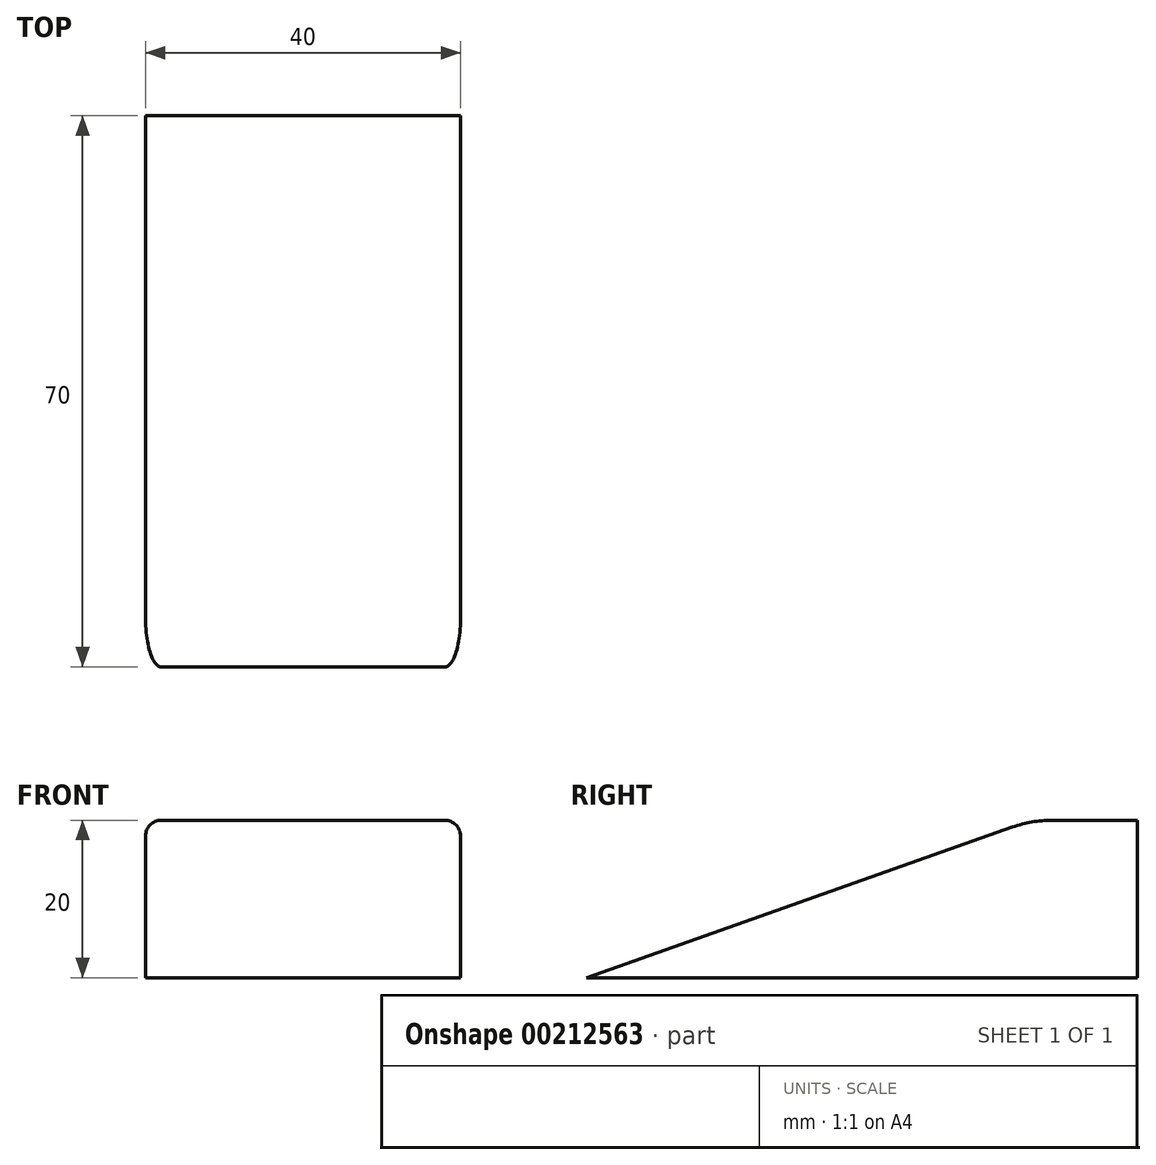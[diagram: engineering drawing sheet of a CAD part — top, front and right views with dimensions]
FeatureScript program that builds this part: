
annotation { "Feature Type Name" : "Feature", "Feature Type Description" : "" }
export const myFeature = defineFeature(function(context is Context, id is Id, definition is map)
    precondition{}
    {
        {
            var Q0;
            Q0=qCreatedBy(makeId("Right.planeOp"),FACE);
            var sketch = newSketch(context, id + "F0", { "sketchPlane" : qUnion([Q0])});
            skLineSegment(sketch, "E0.bottom", {"start": v(20.03, 15.08) * mm, "end": v(33.47, 15.08) * mm});
            skLineSegment(sketch, "E0.top", {"start": v(-36.53, -4.92) * mm, "end": v(33.47, -4.92) * mm});
            skLineSegment(sketch, "E0.right", {"start": v(33.47, 15.08) * mm, "end": v(33.47, -4.92) * mm});
            skLineSegment(sketch, "E1", {"start": v(-36.53, -4.92) * mm, "end": v(20.03, 15.08) * mm});
            skSolve(sketch);
        }
        {
            var Q0;
            Q0=makeQuery(id+"F0.imprint","IMPRINT",FACE,{"disambiguationData":[TD([[makeQuery(id+"F0.imprint","IMPRINT",EDGE,{"derivedFrom":sQuery(id+"F0.wireOp",EDGE,"E0.bottom")}),-1.0]])]});
            extrude(context, id + "F1", {"entities" : qUnion([Q0]), "depth" : 40 * mm});
        }
        {
            var Q0;
            Q0=makeQuery(id+"F1.opExtrude","SWEPT_EDGE",EDGE,{"disambiguationData":[OSD([sQuery(id+"F0.wireOp",EDGE,"E0.bottom"),sQuery(id+"F0.wireOp",EDGE,"E1")])]});
            fillet(context, id + "F2", {"entities" : qUnion([Q0]), "radius" : 15 * mm, "tangentPropagation" : true, "allowEdgeOverflow" : false});
        }
        {
            var Q0;
            Q0=makeQuery(id+"F1.opExtrude","CAP_EDGE",EDGE,{"disambiguationData":[OSD([sQuery(id+"F0.wireOp",EDGE,"E1")])],"isStart":false});
            var Q1;
            Q1=makeQuery(id+"F1.opExtrude","CAP_EDGE",EDGE,{"disambiguationData":[OSD([sQuery(id+"F0.wireOp",EDGE,"E1")])],"isStart":true});
            fillet(context, id + "F3", {"entities" : qUnion([Q0, Q1]), "radius" : 2 * mm, "tangentPropagation" : true, "allowEdgeOverflow" : false});
        }
    });
